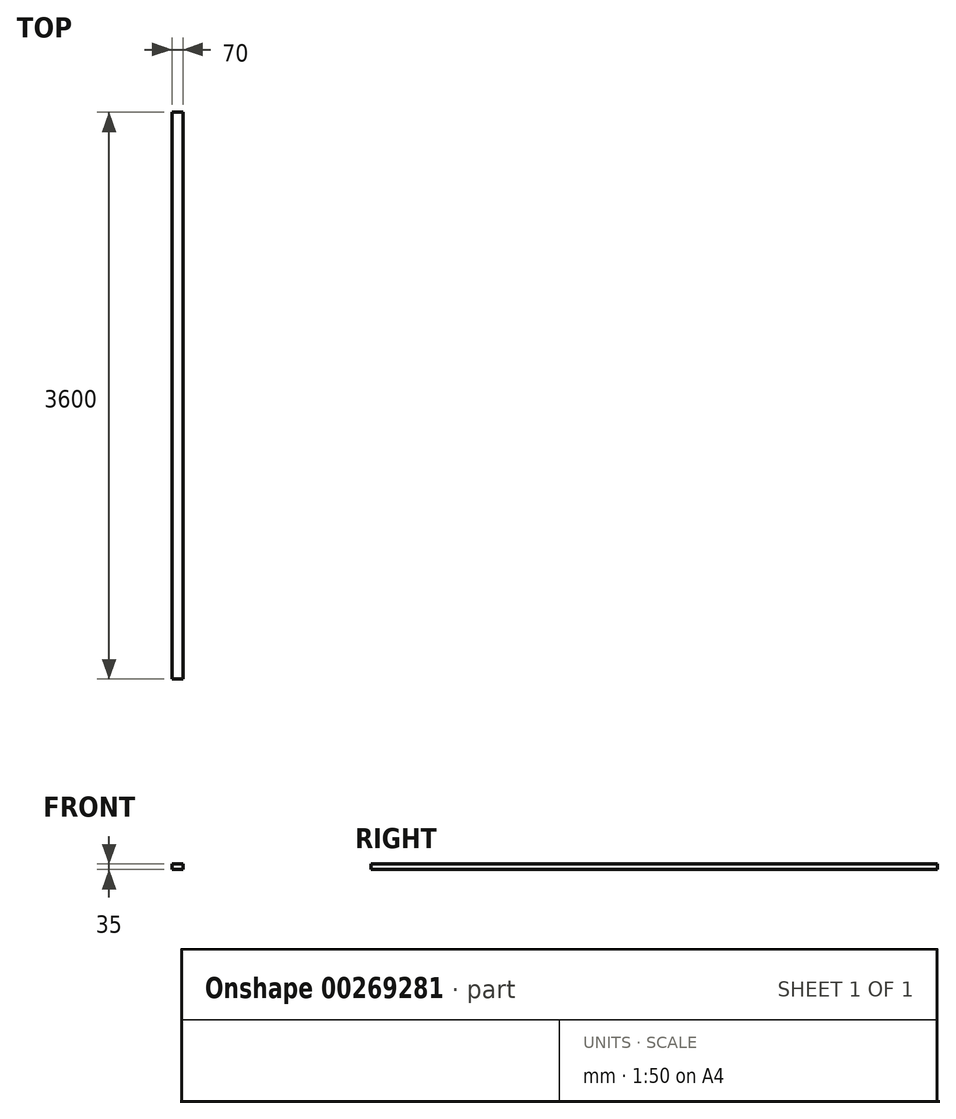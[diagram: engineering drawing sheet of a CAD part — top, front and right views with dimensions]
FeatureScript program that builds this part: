
annotation { "Feature Type Name" : "Feature", "Feature Type Description" : "" }
export const myFeature = defineFeature(function(context is Context, id is Id, definition is map)
    precondition{}
    {
        {
            var Q0;
            Q0=qCreatedBy(makeId("Front.planeOp"),FACE);
            var sketch = newSketch(context, id + "F0", { "sketchPlane" : qUnion([Q0])});
            skLineSegment(sketch, "E0.bottom", {"start": v(-35, 17.26) * mm, "end": v(35, 17.26) * mm});
            skLineSegment(sketch, "E0.top", {"start": v(-35, -17.74) * mm, "end": v(35, -17.74) * mm});
            skLineSegment(sketch, "E0.left", {"start": v(-35, 17.26) * mm, "end": v(-35, -17.74) * mm});
            skLineSegment(sketch, "E0.right", {"start": v(35, 17.26) * mm, "end": v(35, -17.74) * mm});
            skSolve(sketch);
        }
        {
            assignVariable(context, id + "F1", {"name" : "Length", "anyValue" : 3600});
        }
        {
            var Q0;
            Q0=qSketchRegion(id+"F0",true);
            extrude(context, id + "F2", {"entities" : qUnion([Q0]), "depth" : (getVariable(context, 'Length')) * mm});
        }
    });
